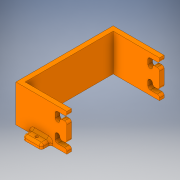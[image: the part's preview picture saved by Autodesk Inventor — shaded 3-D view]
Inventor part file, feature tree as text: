
AUTODESK INVENTOR PART (.ipt)
format: ipt  version: 2019 (Build 230136000, 136)  size: 279,040 bytes
history: native  units: in
note: dims shown in document units (in); Inventor stores cm internally (conversion verified against a paired STEP export)
features: sketch x5, extrude x4, fillet x3, hole x1
ambient origin geometry x8: Origin, YZ Plane, XZ Plane, XY Plane, X Axis, Y Axis, Z Axis, Center Point
bodies: Solid1 (feature_tree)
feature tree (13):
  extrude  "Extrusion1"  Depth=0.25in
  extrude  "Extrusion6"  Depth=4.75in
  fillet  "Fillet4"  Radius=2.5in
  fillet  "Fillet5"  Radius=2.0in
  extrude  "Extrusion7"  Depth=0.25in
  extrude  "Extrusion8"  Depth=0.25in
  fillet  "Fillet6"  Radius=0.5in
  hole  "Hole2"  [1 undecoded]
  sketch  "Sketch1"  dims[d0=0.25in d1=0.25in]
  sketch  "Sketch6"  dims[d2=0.25in d3=4.75in d4=2.5in d5=2.0in d6=0.0in]
  sketch  "Sketch7"  dims[d102=0.25in d104=0.375in]
  sketch  "Sketch8"  dims[d105=0.25in d106=0.25in d107=0.5in]
  sketch  "Sketch9"  dims[d108=0.5in d109=0.25in d110=0.25in d111=6.0in d112=0.0in d114=0.125in d115=0.125in d116=0.25in d117=1.0in d118=0.0in d119=2.75in d120=0.875in d121=0.5in d122=0.0in d123=1.0in d124=0.25in d125=2.75in d126=0.875in d127=0.25in d128=0.5in d129=0.0in d130=0.125in d131=0.25in d132=0.5in d133=0.25in d134=0.5in d135=0.15in d136=0.328in d137=0.279in d138=0.25in d139=0.5635in d140=0.484in d141=0.0in]
note: 1 required parameter value undecoded (feature->parameter linkage not recoverable at this tier; creation-order binding heuristic only, values carry confidence <= 0.55)
